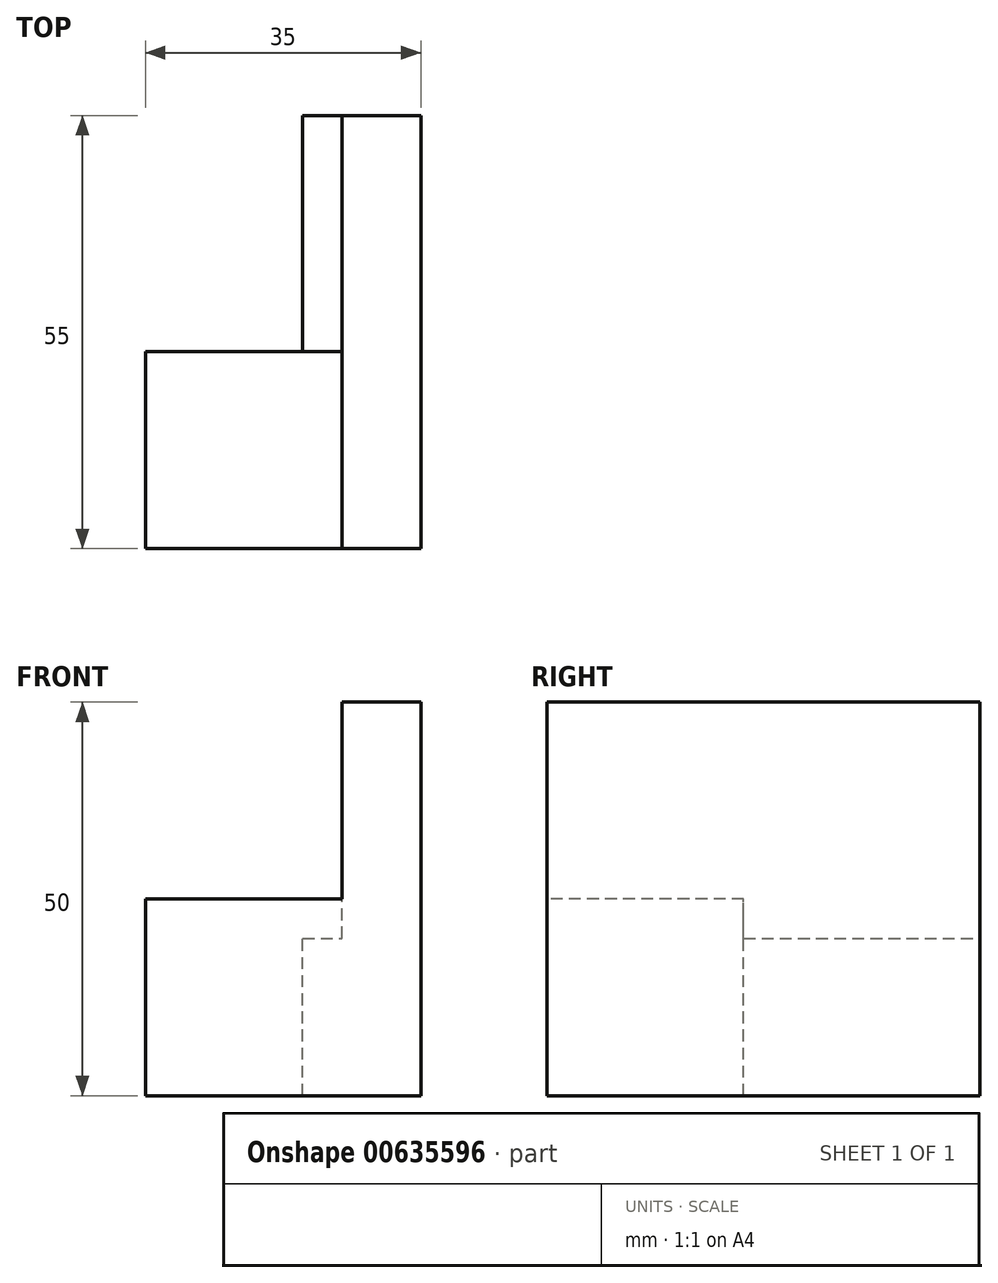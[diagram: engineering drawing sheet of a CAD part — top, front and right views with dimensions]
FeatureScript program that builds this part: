
annotation { "Feature Type Name" : "Feature", "Feature Type Description" : "" }
export const myFeature = defineFeature(function(context is Context, id is Id, definition is map)
    precondition{}
    {
        {
            var Q0;
            Q0=qCreatedBy(makeId("Right.planeOp"),FACE);
            var sketch = newSketch(context, id + "F0", { "sketchPlane" : qUnion([Q0])});
            skLineSegment(sketch, "E0", {"start": v(-44.25, -24) * mm, "end": v(10.75, -24) * mm});
            skLineSegment(sketch, "E1", {"start": v(10.75, -24) * mm, "end": v(10.75, 26) * mm});
            skLineSegment(sketch, "E2", {"start": v(10.75, 26) * mm, "end": v(-44.25, 26) * mm});
            skLineSegment(sketch, "E3", {"start": v(-44.25, 26) * mm, "end": v(-44.25, -24) * mm});
            skSolve(sketch);
        }
        {
            var Q0;
            Q0 = qSketchRegion(id + "F0", true);
            var Q1;
            Q1=makeQuery(id+"F0.imprint","IMPRINT",FACE,{"disambiguationData":[TD([[makeQuery(id+"F0.imprint","IMPRINT",EDGE,{"derivedFrom":sQuery(id+"F0.wireOp",EDGE,"E0")}),1.0]])]});
            extrude(context, id + "F1", {"entities" : qUnion([Q0, Q1]), "depth" : 10 * mm, "offsetDistance" : 25.4 * mm});
        }
        {
            var Q0;
            Q0=makeQuery(id+"F1.opExtrude","CAP_FACE",FACE,{"disambiguationData":[OSD([sQuery(id+"F0.wireOp",EDGE,"E0"),sQuery(id+"F0.wireOp",EDGE,"E1"),sQuery(id+"F0.wireOp",EDGE,"E2"),sQuery(id+"F0.wireOp",EDGE,"E3")])],"isStart":true});
            var sketch = newSketch(context, id + "F2", { "sketchPlane" : qUnion([Q0])});
            skLineSegment(sketch, "E4", {"start": v(44.25, -24) * mm, "end": v(19.25, -24) * mm});
            skLineSegment(sketch, "E5", {"start": v(19.25, -24) * mm, "end": v(19.25, 1) * mm});
            skLineSegment(sketch, "E6", {"start": v(19.25, 1) * mm, "end": v(44.25, 1) * mm});
            skLineSegment(sketch, "E7", {"start": v(44.25, 1) * mm, "end": v(44.25, -24) * mm});
            skSolve(sketch);
        }
        {
            var Q0;
            Q0=makeQuery(id+"F2.imprint","IMPRINT",FACE,{"disambiguationData":[TD([[makeQuery(id+"F2.imprint","IMPRINT",EDGE,{"derivedFrom":sQuery(id+"F2.wireOp",EDGE,"E4")}),-1.0]])]});
            extrude(context, id + "F3", {"entities" : qUnion([Q0]), "operationType" : NewBodyOperationType.ADD, "depth" : 25 * mm, "offsetDistance" : 25.4 * mm});
        }
        {
            var Q0;
            Q0=makeQuery(id+"F1.opExtrude","CAP_FACE",FACE,{"disambiguationData":[OSD([sQuery(id+"F0.wireOp",EDGE,"E0"),sQuery(id+"F0.wireOp",EDGE,"E1"),sQuery(id+"F0.wireOp",EDGE,"E2"),sQuery(id+"F0.wireOp",EDGE,"E3")])],"isStart":true});
            var sketch = newSketch(context, id + "F4", { "sketchPlane" : qUnion([Q0])});
            skLineSegment(sketch, "E8", {"start": v(-10.75, -24) * mm, "end": v(19.25, -24) * mm});
            skLineSegment(sketch, "E9", {"start": v(19.25, -24) * mm, "end": v(19.25, -4) * mm});
            skLineSegment(sketch, "E10", {"start": v(19.25, -4) * mm, "end": v(-10.75, -4) * mm});
            skLineSegment(sketch, "E11", {"start": v(-10.75, -4) * mm, "end": v(-10.75, -24) * mm});
            skSolve(sketch);
        }
        {
            var Q0;
            Q0=makeQuery(id+"F4.imprint","IMPRINT",FACE,{"disambiguationData":[TD([[makeQuery(id+"F4.imprint","IMPRINT",EDGE,{"derivedFrom":sQuery(id+"F4.wireOp",EDGE,"E8")}),-1.0]])]});
            extrude(context, id + "F5", {"entities" : qUnion([Q0]), "operationType" : NewBodyOperationType.ADD, "depth" : 5 * mm, "offsetDistance" : 25.4 * mm});
        }
    });
